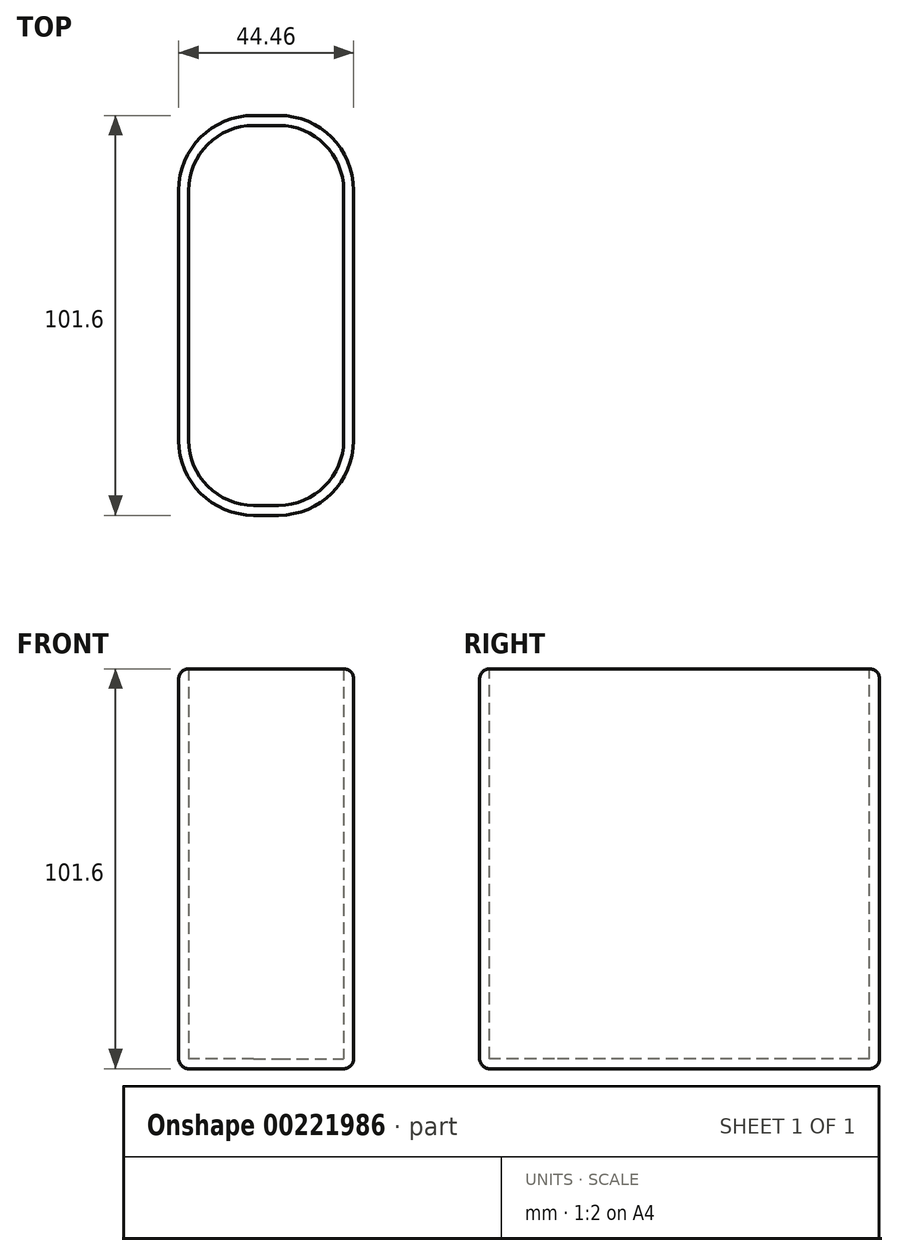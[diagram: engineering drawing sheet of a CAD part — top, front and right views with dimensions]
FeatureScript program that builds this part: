
annotation { "Feature Type Name" : "Feature", "Feature Type Description" : "" }
export const myFeature = defineFeature(function(context is Context, id is Id, definition is map)
    precondition{}
    {
        {
            var Q0;
            Q0=qCreatedBy(makeId("Top.planeOp"),FACE);
            var sketch = newSketch(context, id + "F0", { "sketchPlane" : qUnion([Q0])});
            skLineSegment(sketch, "E0.bottom", {"start": v(-22.22, 50.8) * mm, "end": v(22.23, 50.8) * mm});
            skLineSegment(sketch, "E0.top", {"start": v(-22.23, -50.8) * mm, "end": v(22.22, -50.8) * mm});
            skLineSegment(sketch, "E0.left", {"start": v(-22.22, 50.8) * mm, "end": v(-22.23, -50.8) * mm});
            skLineSegment(sketch, "E0.right", {"start": v(22.23, 50.8) * mm, "end": v(22.22, -50.8) * mm});
            skPoint(sketch, "E0.middle", {"position": v(0, 0) * mm});
            skSolve(sketch);
        }
        {
            var Q0;
            Q0=makeQuery(id+"F0.imprint","IMPRINT",FACE,{"disambiguationData":[TD([[makeQuery(id+"F0.imprint","IMPRINT",EDGE,{"derivedFrom":sQuery(id+"F0.wireOp",EDGE,"E0.bottom")}),-1.0]])]});
            extrude(context, id + "F1", {"entities" : qUnion([Q0]), "depth" : 101.6 * mm});
        }
        {
            var Q0;
            Q0=makeQuery(id+"F1.opExtrude","SWEPT_EDGE",EDGE,{"disambiguationData":[OSD([sQuery(id+"F0.wireOp",EDGE,"E0.bottom"),sQuery(id+"F0.wireOp",EDGE,"E0.left")])]});
            var Q1;
            Q1=makeQuery(id+"F1.opExtrude","SWEPT_EDGE",EDGE,{"disambiguationData":[OSD([sQuery(id+"F0.wireOp",EDGE,"E0.top"),sQuery(id+"F0.wireOp",EDGE,"E0.left")])]});
            var Q2;
            Q2=makeQuery(id+"F1.opExtrude","SWEPT_EDGE",EDGE,{"disambiguationData":[OSD([sQuery(id+"F0.wireOp",EDGE,"E0.top"),sQuery(id+"F0.wireOp",EDGE,"E0.right")])]});
            var Q3;
            Q3=makeQuery(id+"F1.opExtrude","SWEPT_EDGE",EDGE,{"disambiguationData":[OSD([sQuery(id+"F0.wireOp",EDGE,"E0.bottom"),sQuery(id+"F0.wireOp",EDGE,"E0.right")])]});
            fillet(context, id + "F2", {"entities" : qUnion([Q0, Q1, Q2, Q3]), "radius" : 19.05 * mm, "tangentPropagation" : true, "allowEdgeOverflow" : false});
        }
        {
            var Q0;
            Q0=makeQuery(id+"F1.opExtrude","CAP_FACE",FACE,{"disambiguationData":[OSD([sQuery(id+"F0.wireOp",EDGE,"E0.bottom"),sQuery(id+"F0.wireOp",EDGE,"E0.top"),sQuery(id+"F0.wireOp",EDGE,"E0.left"),sQuery(id+"F0.wireOp",EDGE,"E0.right")])],"isStart":false});
            shell(context, id + "F3", {"entities" : qUnion([Q0]), "thickness" : 2.54 * mm});
        }
        {
            var Q0;
            Q0=makeQuery(id+"F1.opExtrude","SWEPT_FACE",FACE,{"disambiguationData":[OSD([sQuery(id+"F0.wireOp",EDGE,"E0.right")])]});
            var Q1;
            Q1=makeQuery(id+"F1.opExtrude","SWEPT_FACE",FACE,{"disambiguationData":[OSD([sQuery(id+"F0.wireOp",EDGE,"E0.left")])]});
            fillet(context, id + "F4", {"entities" : qUnion([Q0, Q1]), "radius" : 2.54 * mm, "tangentPropagation" : true, "allowEdgeOverflow" : false});
        }
    });
